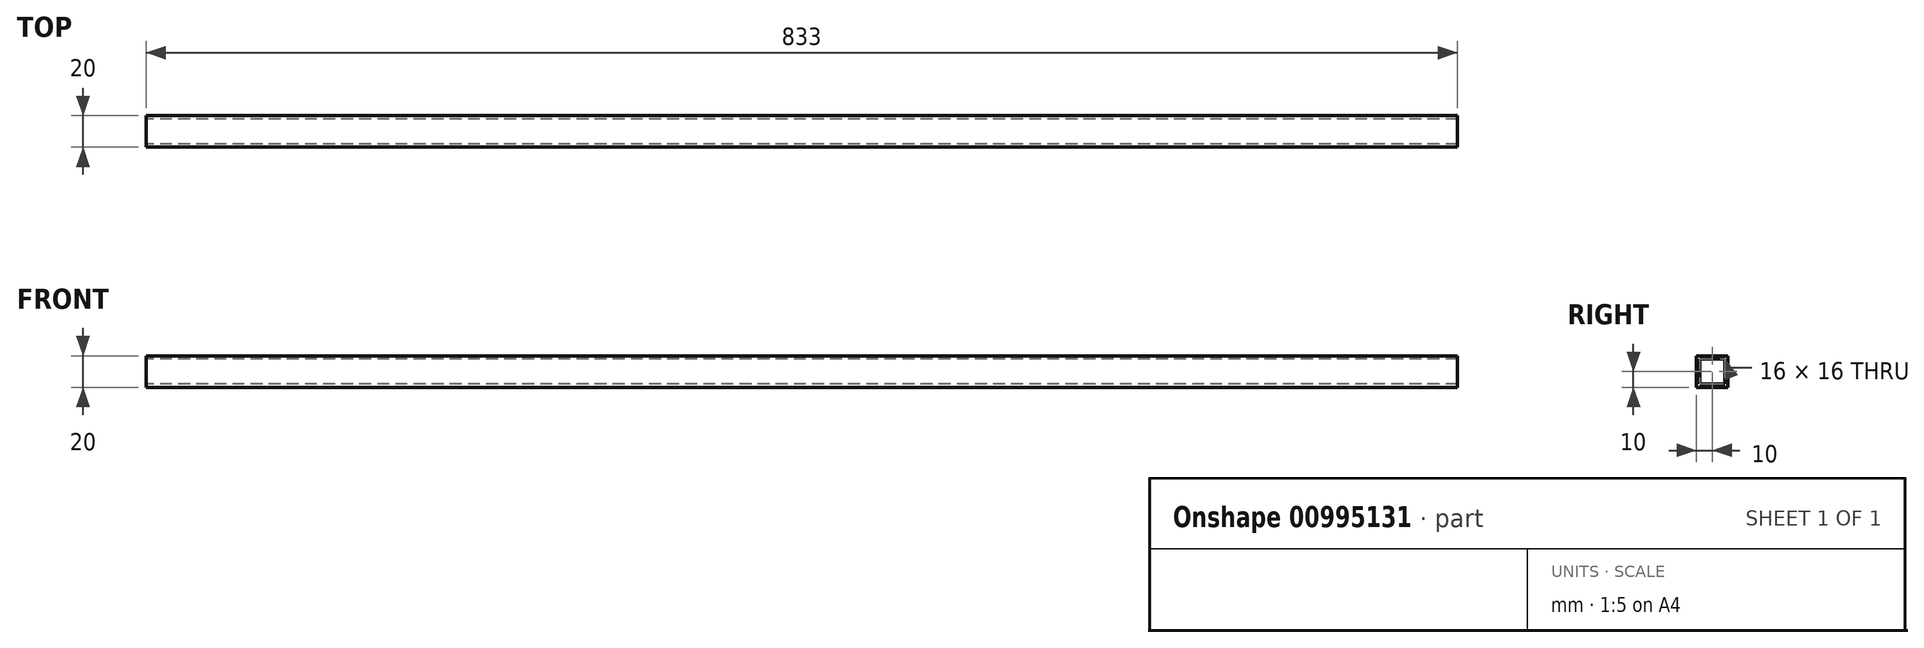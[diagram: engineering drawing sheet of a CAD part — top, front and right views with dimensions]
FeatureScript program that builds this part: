
annotation { "Feature Type Name" : "Feature", "Feature Type Description" : "" }
export const myFeature = defineFeature(function(context is Context, id is Id, definition is map)
    precondition{}
    {
        {
            var Q0;
            Q0=qCreatedBy(makeId("Right.planeOp"),FACE);
            var sketch = newSketch(context, id + "F0", { "sketchPlane" : qUnion([Q0])});
            skLineSegment(sketch, "E0.bottom", {"start": v(0, 0) * mm, "end": v(-20, 0) * mm});
            skLineSegment(sketch, "E0.top", {"start": v(0, 20) * mm, "end": v(-20, 20) * mm});
            skLineSegment(sketch, "E0.left", {"start": v(0, 0) * mm, "end": v(0, 20) * mm});
            skLineSegment(sketch, "E0.right", {"start": v(-20, 0) * mm, "end": v(-20, 20) * mm});
            skLineSegment(sketch, "E1.0", {"start": v(-2, 2) * mm, "end": v(-2, 18) * mm});
            skLineSegment(sketch, "E1.1", {"start": v(-2, 2) * mm, "end": v(-18, 2) * mm});
            skLineSegment(sketch, "E1.2", {"start": v(-18, 2) * mm, "end": v(-18, 18) * mm});
            skLineSegment(sketch, "E1.3", {"start": v(-2, 18) * mm, "end": v(-18, 18) * mm});
            skSolve(sketch);
        }
        {
            var Q0;
            Q0 = qSketchRegion(id + "F0", true);
            extrude(context, id + "F1", {"entities" : qUnion([Q0]), "depth" : 833 * mm, "offsetDistance" : 25 * mm});
        }
    });
